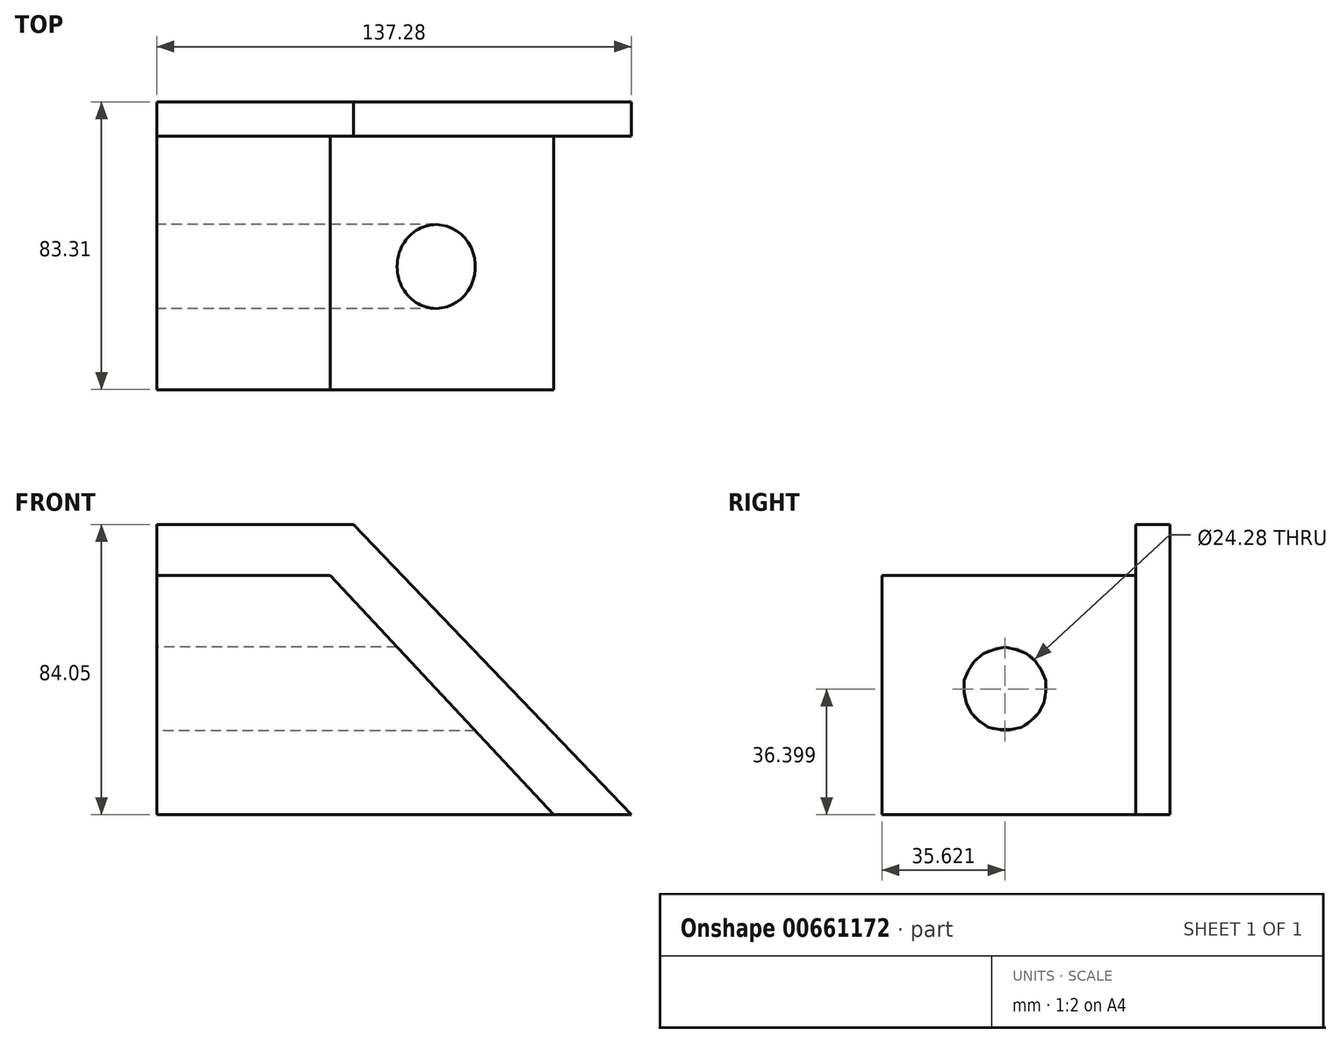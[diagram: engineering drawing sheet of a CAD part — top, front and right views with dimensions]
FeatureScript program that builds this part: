
annotation { "Feature Type Name" : "Feature", "Feature Type Description" : "" }
export const myFeature = defineFeature(function(context is Context, id is Id, definition is map)
    precondition{}
    {
        {
            var Q0;
            Q0=qCreatedBy(makeId("Front.planeOp"),FACE);
            var sketch = newSketch(context, id + "F0", { "sketchPlane" : qUnion([Q0])});
            skLineSegment(sketch, "E0", {"start": v(0, 0) * mm, "end": v(0, 84.05) * mm});
            skLineSegment(sketch, "E1", {"start": v(0, 84.05) * mm, "end": v(56.93, 84.05) * mm});
            skLineSegment(sketch, "E2", {"start": v(56.93, 84.05) * mm, "end": v(137.28, 0) * mm});
            skLineSegment(sketch, "E3", {"start": v(137.28, 0) * mm, "end": v(0, 0) * mm});
            skLineSegment(sketch, "E4", {"start": v(0, 69.28) * mm, "end": v(50.11, 69.28) * mm});
            skLineSegment(sketch, "E5", {"start": v(50.11, 69.28) * mm, "end": v(114.85, 0) * mm});
            skSolve(sketch);
        }
        {
            var Q0;
            {var subQ3=sQuery(id+"F0.wireOp",EDGE,"E4");Q0=makeQuery(id+"F0.imprint","IMPRINT",FACE,{"disambiguationData":[TD([[makeQuery(id+"F0.imprint","IMPRINT",EDGE,{"derivedFrom":subQ3}),-1.0]])]});}
            extrude(context, id + "F1", {"entities" : qUnion([Q0]), "depth" : 83.31 * mm, "offsetDistance" : 25.4 * mm});
        }
        {
            var Q0;
            {var subQ3=sQuery(id+"F0.wireOp",EDGE,"E1");Q0=makeQuery(id+"F0.imprint","IMPRINT",FACE,{"disambiguationData":[TD([[makeQuery(id+"F0.imprint","IMPRINT",EDGE,{"derivedFrom":subQ3}),-1.0]])]});}
            extrude(context, id + "F2", {"entities" : qUnion([Q0]), "operationType" : NewBodyOperationType.ADD, "depth" : 9.9 * mm, "offsetDistance" : 25.4 * mm});
        }
        {
            var Q0;
            Q0=qCreatedBy(makeId("Right.planeOp"),FACE);
            var sketch = newSketch(context, id + "F3", { "sketchPlane" : qUnion([Q0])});
            skCircle(sketch, "E6", {"center": v(-47.69, 36.4) * mm, "radius": 12.14 * mm});
            skSolve(sketch);
        }
        {
            var Q0;
            Q0=qSketchRegion(id+"F3",true);
            extrude(context, id + "F4", {"entities" : qUnion([Q0]), "operationType" : NewBodyOperationType.REMOVE, "depth" : 170.94 * mm, "offsetDistance" : 25.4 * mm});
        }
    });
